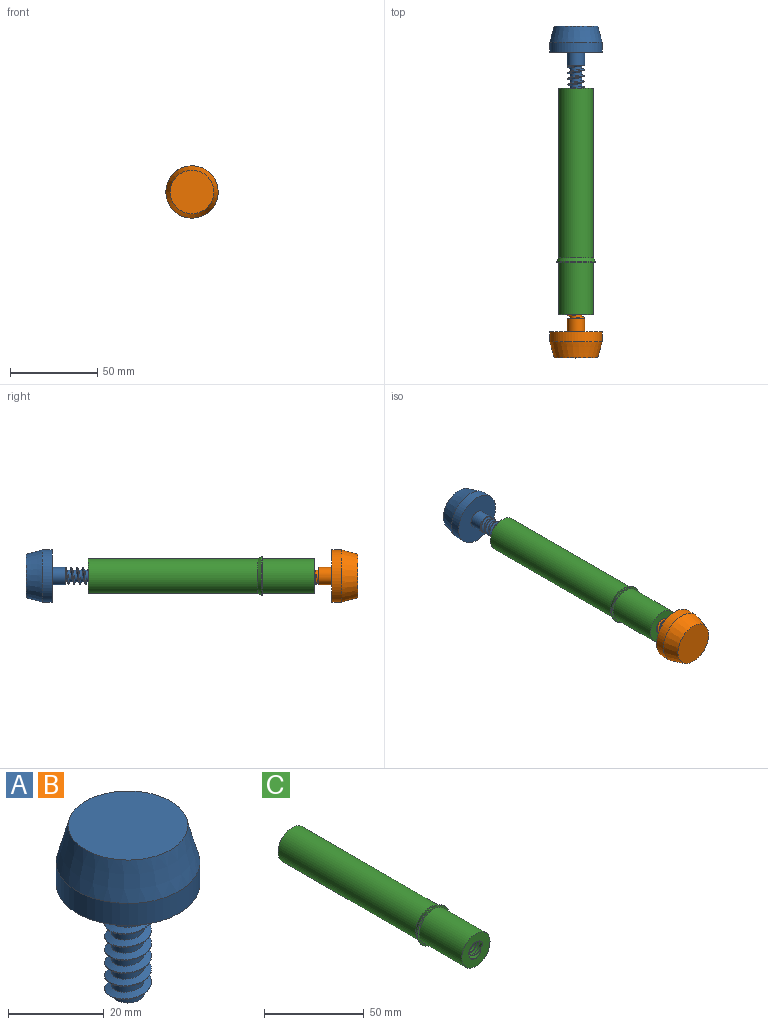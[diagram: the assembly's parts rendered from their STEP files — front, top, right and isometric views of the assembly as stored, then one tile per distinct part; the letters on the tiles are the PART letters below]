
ASSEMBLY  parts=3 mates=1
PART A: 12 faces, bbox 30x30x43.8 mm
  f0: plane 30x30mm, normal (0,0,-1), area 628.3mm2, adj f1,f4
  f1: cylinder r=15mm len=30mm, axis (0,0,-1), area 534.4mm2, adj f0,f3
  f2: plane 25x25mm, normal (0,0,1), area 490.9mm2, adj f3
  f3: cone r=12.5mm half-angle=15deg, axis (0,0,-1), area 834.5mm2, adj f1,f2
  f4: cylinder r=5mm len=10mm, axis (0,0,1), area 235.6mm2, adj f0,f5
  f5: plane 10x10mm, normal (0,0,-1), area 32.8mm2, adj f4,f8,f9,f10,f11
  f6: plane 1.49x0.75mm, normal (0,-1,0), area 0.6mm2, adj f7,f9,f10,f11
  f7: plane 8.29x6.83mm, normal (0,0,-1), area 41.1mm2, adj f6,f8,f10,f11
  f8: bspline ~22.32x11.3mm, area 262.4mm2, adj f5,f7,f10,f11
  f9: bspline ~21.21x11.3mm, area 257.6mm2, adj f5,f6,f10,f11
  f10: cylinder r=4.89mm len=20.5mm, axis (0,0,1), area 42.5mm2, adj f5,f6,f7,f8,f9
  f11: cylinder r=3.4mm len=20.5mm, axis (0,0,1), area 242.7mm2, adj f5,f6,f7,f8,f9
PART B: same geometry as A
PART C: 22 faces, bbox 22.9x131.9x22.9 mm
  f0: plane 1.49x0.75mm, normal (0,0,1), area 0.6mm2, adj f2,f4,f9,f13
  f1: bspline ~20.65x11.55mm, area 256.9mm2, adj f2,f4,f9,f12
  f2: cylinder r=3.51mm len=20.1mm, axis (0,1,0), area 24.8mm2, adj f0,f1,f9,f12,f13
  f3: cone r=0mm half-angle=59deg, axis (0,-1,0), area 88.8mm2, adj f4,f12,f13
  f4: cylinder r=5mm len=20mm, axis (0,-1,0), area 348.3mm2, adj f0,f1,f3,f9,f12,f13
  f5: cylinder r=10mm len=97.5mm, axis (0,1,0), area 6126.1mm2, adj f7,f21
  f6: cylinder r=11.25mm len=22.5mm, axis (0,-1,0), area 35.3mm2, adj f8,f11
  f7: plane 20x20mm, normal (0,1,0), area 0mm2, adj f5,f11
  f8: plane 22.5x22.5mm, normal (0,-1,0), area 83.4mm2, adj f6,f10
  f9: plane 20.38x20.38mm, normal (0,-1,0), area 240.9mm2, adj f0,f1,f2,f4,f10
  f10: cylinder r=10mm len=30mm, axis (0,1,0), area 1885mm2, adj f8,f9
  f11: cone r=11.25mm half-angle=32deg, axis (0,-1,0), area 157.4mm2, adj f6,f7
  f12: plane 1.49x1.19mm, normal (0,0,-1), area 1mm2, adj f1,f2,f3,f4,f13
  f13: bspline ~20.65x11.55mm, area 259.9mm2, adj f0,f2,f3,f4,f12
  f14: plane 1.49x1.19mm, normal (0,0,-1), area 1mm2, adj f15,f16,f18,f19,f20
  f15: cone r=0mm half-angle=59deg, axis (0,1,0), area 88.8mm2, adj f14,f16,f20
  f16: bspline ~20.65x11.55mm, area 259.9mm2, adj f14,f15,f17,f18,f20
  f17: plane 1.49x0.75mm, normal (0,0,1), area 0.6mm2, adj f16,f18,f20,f21
  f18: cylinder r=3.51mm len=20.1mm, axis (0,-1,0), area 26.4mm2, adj f14,f16,f17,f19,f21
  f19: bspline ~20.65x11.55mm, area 256.9mm2, adj f14,f18,f20,f21
  f20: cylinder r=5mm len=20mm, axis (0,1,0), area 348.3mm2, adj f14,f15,f16,f17,f19,f21
  f21: plane 20.38x20.38mm, normal (0,1,0), area 240.9mm2, adj f5,f17,f18,f19,f20
PLACE A rot(axis=(-0.36,-0.66,-0.66),140.3deg) t=(0.3,154.4,-0.74)mm
PLACE B rot(axis=(1,0,0),90deg) t=(0.3,-6.29,-0.74)mm
PLACE C rot(axis=(0,1,0),0deg) t=(0.3,68.68,-0.74)mm
MATE cylindrical A.f10 <-> C.f2  axis (0,1,0) through (0.3,146.9,-0.74)mm
